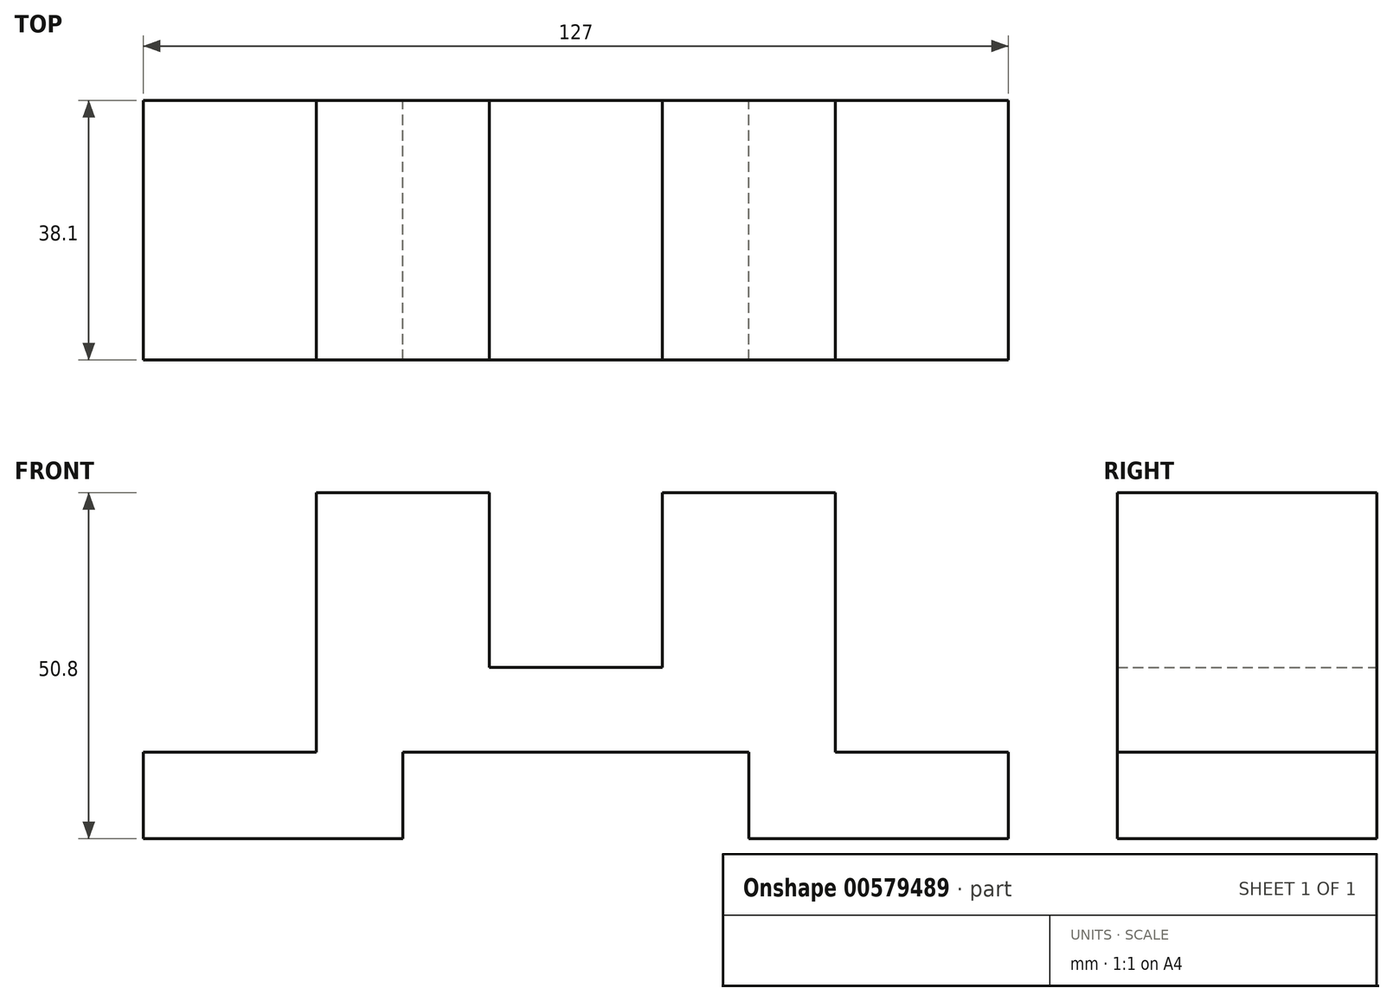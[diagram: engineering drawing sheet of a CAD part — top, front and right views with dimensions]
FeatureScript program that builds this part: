
annotation { "Feature Type Name" : "Feature", "Feature Type Description" : "" }
export const myFeature = defineFeature(function(context is Context, id is Id, definition is map)
    precondition{}
    {
        {
            var Q0;
            Q0=qCreatedBy(makeId("Front.planeOp"),FACE);
            var sketch = newSketch(context, id + "F0", { "sketchPlane" : qUnion([Q0])});
            skLineSegment(sketch, "E0", {"start": v(-66.2, -25.14) * mm, "end": v(-28.1, -25.14) * mm});
            skLineSegment(sketch, "E1", {"start": v(-28.1, -25.14) * mm, "end": v(-28.1, -12.44) * mm});
            skLineSegment(sketch, "E2", {"start": v(-28.1, -12.44) * mm, "end": v(22.7, -12.44) * mm});
            skLineSegment(sketch, "E3", {"start": v(22.7, -12.44) * mm, "end": v(22.7, -25.14) * mm});
            skLineSegment(sketch, "E4", {"start": v(22.7, -25.14) * mm, "end": v(60.8, -25.14) * mm});
            skLineSegment(sketch, "E5", {"start": v(60.8, -25.14) * mm, "end": v(60.8, -12.44) * mm});
            skLineSegment(sketch, "E6", {"start": v(60.8, -12.44) * mm, "end": v(35.4, -12.44) * mm});
            skLineSegment(sketch, "E7", {"start": v(35.4, -12.44) * mm, "end": v(35.4, 25.66) * mm});
            skLineSegment(sketch, "E8", {"start": v(35.4, 25.66) * mm, "end": v(10, 25.66) * mm});
            skLineSegment(sketch, "E9", {"start": v(10, 25.66) * mm, "end": v(10, 0) * mm});
            skLineSegment(sketch, "E10", {"start": v(10, 0) * mm, "end": v(-15.4, 0) * mm});
            skLineSegment(sketch, "E11", {"start": v(-15.4, 0) * mm, "end": v(-15.4, 25.66) * mm});
            skLineSegment(sketch, "E12", {"start": v(-15.4, 25.66) * mm, "end": v(-40.8, 25.66) * mm});
            skLineSegment(sketch, "E13", {"start": v(-40.8, 25.66) * mm, "end": v(-40.8, -12.44) * mm});
            skLineSegment(sketch, "E14", {"start": v(-40.8, -12.44) * mm, "end": v(-66.2, -12.44) * mm});
            skLineSegment(sketch, "E15", {"start": v(-66.2, -12.44) * mm, "end": v(-66.2, -25.14) * mm});
            skSolve(sketch);
        }
        {
            var Q0;
            Q0 = qSketchRegion(id + "F0", true);
            extrude(context, id + "F1", {"entities" : qUnion([Q0]), "depth" : 38.1 * mm, "offsetDistance" : 25.4 * mm});
        }
    });
